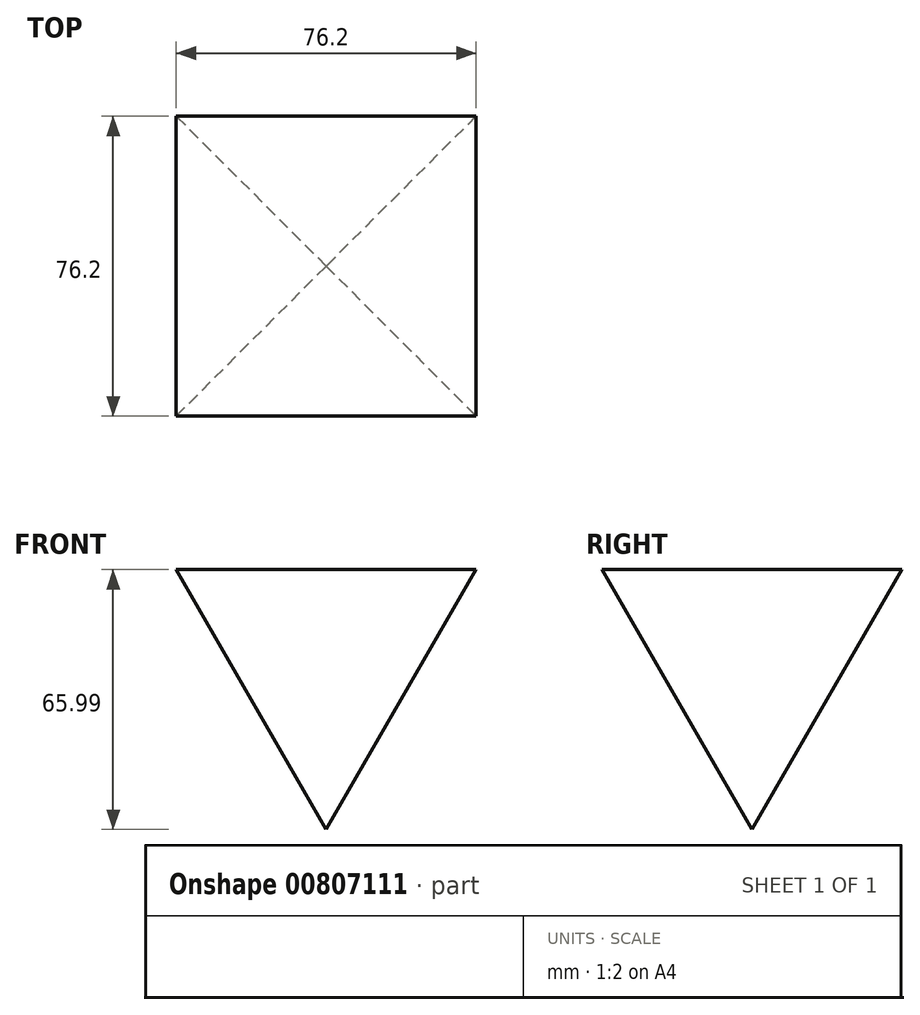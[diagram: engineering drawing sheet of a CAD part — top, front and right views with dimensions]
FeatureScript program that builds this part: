
annotation { "Feature Type Name" : "Feature", "Feature Type Description" : "" }
export const myFeature = defineFeature(function(context is Context, id is Id, definition is map)
    precondition{}
    {
        {
            var Q0;
            Q0=qCreatedBy(makeId("Top.planeOp"),FACE);
            var sketch = newSketch(context, id + "F0", { "sketchPlane" : qUnion([Q0])});
            skLineSegment(sketch, "E0.bottom", {"start": v(-72.45, -76.95) * mm, "end": v(3.75, -76.95) * mm});
            skLineSegment(sketch, "E0.top", {"start": v(-72.45, -0.75) * mm, "end": v(3.75, -0.75) * mm});
            skLineSegment(sketch, "E0.left", {"start": v(-72.45, -76.95) * mm, "end": v(-72.45, -0.75) * mm});
            skLineSegment(sketch, "E0.right", {"start": v(3.75, -76.95) * mm, "end": v(3.75, -0.75) * mm});
            skSolve(sketch);
        }
        {
            var Q0;
            Q0=makeQuery(id+"F0.imprint","IMPRINT",FACE,{"disambiguationData":[TD([[makeQuery(id+"F0.imprint","IMPRINT",EDGE,{"derivedFrom":sQuery(id+"F0.wireOp",EDGE,"E0.bottom")}),1.0]])]});
            extrude(context, id + "F1", {"entities" : qUnion([Q0]), "oppositeDirection" : true, "depth" : 69.1 * mm, "offsetDistance" : 25.4 * mm, "hasDraft" : true, "draftAngle" : 30 * degree, "draftPullDirection" : true});
        }
    });
